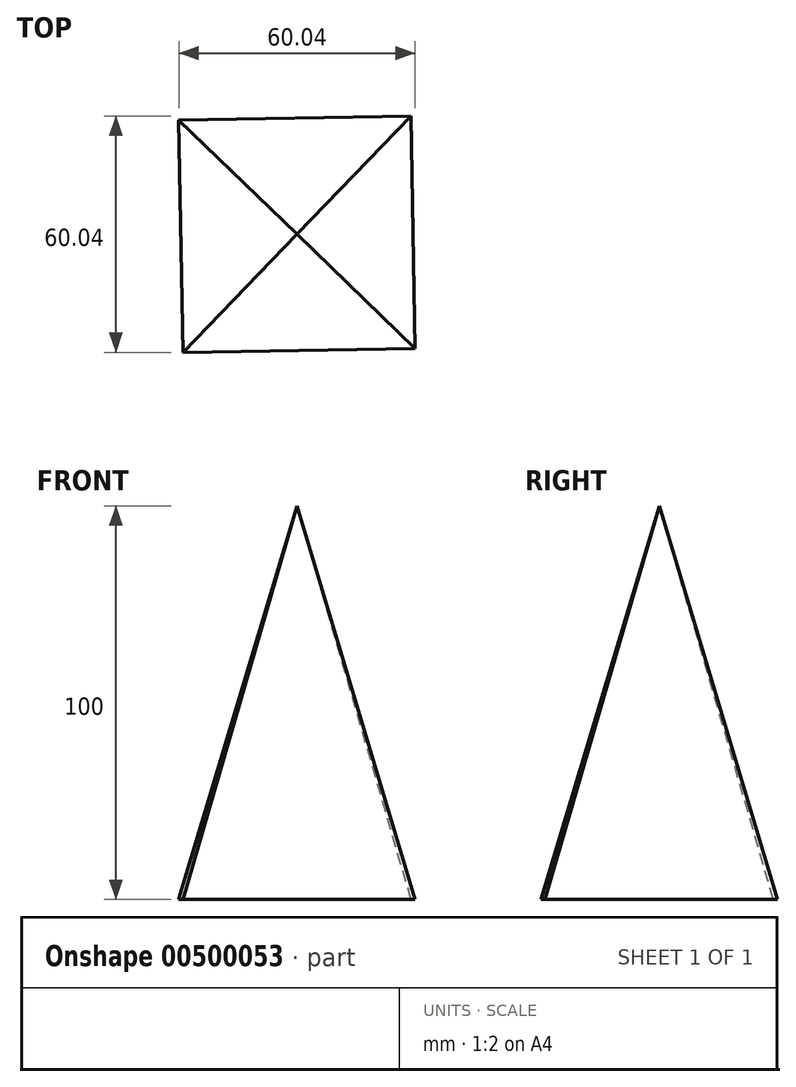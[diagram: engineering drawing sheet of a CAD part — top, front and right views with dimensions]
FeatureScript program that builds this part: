
annotation { "Feature Type Name" : "Feature", "Feature Type Description" : "" }
export const myFeature = defineFeature(function(context is Context, id is Id, definition is map)
    precondition{}
    {
        {
            var Q0;
            Q0=qCreatedBy(makeId("Top.planeOp"),FACE);
            var sketch = newSketch(context, id + "F0", { "sketchPlane" : qUnion([Q0])});
            skCircle(sketch, "E0.cCircle", {"center": v(0, 0) * mm, "radius": 41.74 * mm, "construction": true});
            skLineSegment(sketch, "E0.0", {"start": v(29, 30.02) * mm, "end": v(30.02, -29) * mm});
            skLineSegment(sketch, "E0.1", {"start": v(30.02, -29) * mm, "end": v(-29, -30.02) * mm});
            skLineSegment(sketch, "E0.2", {"start": v(-29, -30.02) * mm, "end": v(-30.02, 29) * mm});
            skLineSegment(sketch, "E0.3", {"start": v(-30.02, 29) * mm, "end": v(29, 30.02) * mm});
            skSolve(sketch);
        }
        {
            var Q0;
            Q0=qCreatedBy(makeId("Top.planeOp"),FACE);
            cPlane(context, id + "F1", {"entities" : qUnion([Q0]), "cplaneType" : CPlaneType.OFFSET, "offset" : 100 * mm, "width" : 152.4 * mm, "height" : 152.4 * mm});
        }
        {
            var Q0;
            Q0=qCreatedBy(id+"F1.planeOp",FACE);
            var sketch = newSketch(context, id + "F2", { "sketchPlane" : qUnion([Q0])});
            skPoint(sketch, "E1", {"position": v(0, 0) * mm});
            skSolve(sketch);
        }
        {
            var Q0;
            Q0=makeQuery(id+"F0.imprint","IMPRINT",FACE,{"disambiguationData":[TD([[makeQuery(id+"F0.imprint","IMPRINT",EDGE,{"derivedFrom":sQuery(id+"F0.wireOp",EDGE,"E0.0")}),-1.0]])]});
            var Q1;
            Q1=sQuery(id+"F2.wireOp",VERTEX,"E1");
            loft(context, id + "F3", {"sheetProfilesArray" : [{ "sheetProfileEntities" : qUnion([Q0]) }, { "sheetProfileEntities" : qUnion([Q1]) }]});
        }
    });
